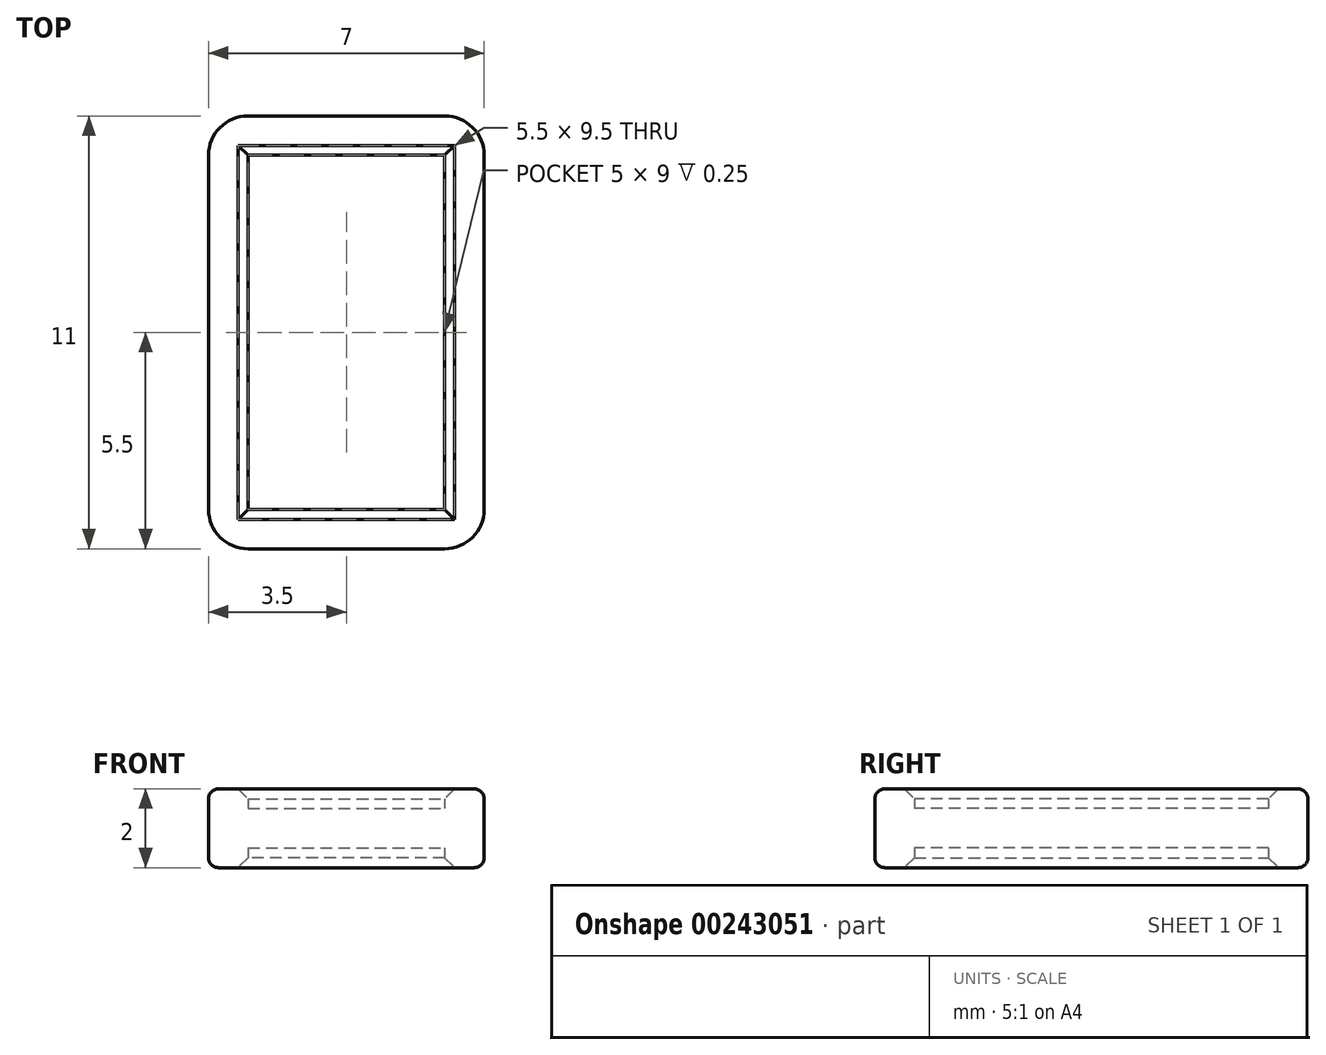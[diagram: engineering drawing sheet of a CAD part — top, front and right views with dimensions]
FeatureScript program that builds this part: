
annotation { "Feature Type Name" : "Feature", "Feature Type Description" : "" }
export const myFeature = defineFeature(function(context is Context, id is Id, definition is map)
    precondition{}
    {
        {
            var Q0;
            Q0=qCreatedBy(makeId("Top.planeOp"),FACE);
            var sketch = newSketch(context, id + "F0", { "sketchPlane" : qUnion([Q0])});
            skLineSegment(sketch, "E0.bottom", {"start": v(0, 0) * mm, "end": v(6, 0) * mm});
            skLineSegment(sketch, "E0.top", {"start": v(0, 10) * mm, "end": v(6, 10) * mm});
            skLineSegment(sketch, "E0.left", {"start": v(0, 0) * mm, "end": v(0, 10) * mm});
            skLineSegment(sketch, "E0.right", {"start": v(6, 0) * mm, "end": v(6, 10) * mm});
            skSolve(sketch);
        }
        {
            var Q0;
            Q0=makeQuery(id+"F0.imprint","IMPRINT",FACE,{"disambiguationData":[TD([[makeQuery(id+"F0.imprint","IMPRINT",EDGE,{"derivedFrom":sQuery(id+"F0.wireOp",EDGE,"E0.bottom")}),1.0]])]});
            extrude(context, id + "F1", {"entities" : qUnion([Q0]), "depth" : 1 * mm});
        }
        {
            var Q0;
            Q0=makeQuery(id+"F1.opExtrude","SWEPT_EDGE",EDGE,{"disambiguationData":[OSD([sQuery(id+"F0.wireOp",EDGE,"E0.bottom"),sQuery(id+"F0.wireOp",EDGE,"E0.right")])]});
            var Q1;
            Q1=makeQuery(id+"F1.opExtrude","SWEPT_EDGE",EDGE,{"disambiguationData":[OSD([sQuery(id+"F0.wireOp",EDGE,"E0.bottom"),sQuery(id+"F0.wireOp",EDGE,"E0.left")])]});
            var Q2;
            Q2=makeQuery(id+"F1.opExtrude","SWEPT_EDGE",EDGE,{"disambiguationData":[OSD([sQuery(id+"F0.wireOp",EDGE,"E0.top"),sQuery(id+"F0.wireOp",EDGE,"E0.right")])]});
            var Q3;
            Q3=makeQuery(id+"F1.opExtrude","SWEPT_EDGE",EDGE,{"disambiguationData":[OSD([sQuery(id+"F0.wireOp",EDGE,"E0.top"),sQuery(id+"F0.wireOp",EDGE,"E0.left")])]});
            fillet(context, id + "F2", {"entities" : qUnion([Q0, Q1, Q2, Q3]), "radius" : 0.5 * mm, "tangentPropagation" : true, "allowEdgeOverflow" : false});
        }
        {
            var Q0;
            Q0=qCreatedBy(makeId("Front.planeOp"),FACE);
            cPlane(context, id + "F3", {"entities" : qUnion([Q0]), "cplaneType" : CPlaneType.OFFSET, "offset" : 0.5 * mm, "oppositeDirection" : true, "width" : 150 * mm, "height" : 150 * mm});
        }
        {
            var Q0;
            Q0=qCreatedBy(id+"F3.planeOp",FACE);
            var sketch = newSketch(context, id + "F4", { "sketchPlane" : qUnion([Q0])});
            skLineSegment(sketch, "E1.0", {"start": v(5.5, 1) * mm, "end": v(6, 1) * mm});
            skLineSegment(sketch, "E1.1", {"start": v(6, 1) * mm, "end": v(6, 0) * mm});
            skLineSegment(sketch, "E1.2", {"start": v(6, 0) * mm, "end": v(5.5, 0) * mm});
            skLineSegment(sketch, "E2.0", {"start": v(6.5, -0.5) * mm, "end": v(5.5, -0.5) * mm});
            skLineSegment(sketch, "E2.1", {"start": v(6.5, 1.5) * mm, "end": v(6.5, -0.5) * mm});
            skLineSegment(sketch, "E2.2", {"start": v(5.5, 1.5) * mm, "end": v(6.5, 1.5) * mm});
            skLineSegment(sketch, "E3", {"start": v(5.5, 1.5) * mm, "end": v(5.5, 1) * mm});
            skLineSegment(sketch, "E4", {"start": v(5.5, 0) * mm, "end": v(5.5, -0.5) * mm});
            skSolve(sketch);
        }
        {
            var Q0;
            Q0=makeQuery(id+"F4.imprint","IMPRINT",FACE,{"disambiguationData":[TD([[makeQuery(id+"F4.imprint","IMPRINT",EDGE,{"derivedFrom":sQuery(id+"F4.wireOp",EDGE,"E1.0")}),1.0]])]});
            var Q1;
            {var subQ0=sQuery(id+"F0.wireOp",EDGE,"E0.right");var subQ1=sQuery(id+"F0.wireOp",EDGE,"E0.bottom");Q1=makeQuery(id+"F2.opFillet","BLEND_EDGE",EDGE,{"blendedFrom":[makeQuery(id+"F1.opExtrude","SWEPT_EDGE",EDGE,{"disambiguationData":[OSD([subQ1,subQ0])]}),makeQuery(id+"F1.opExtrude","CAP_FACE",FACE,{"disambiguationData":[OSD([subQ1,sQuery(id+"F0.wireOp",EDGE,"E0.top"),sQuery(id+"F0.wireOp",EDGE,"E0.left"),subQ0])],"isStart":false})],"blendedInto":[makeQuery(id+"F1.opExtrude","CAP_FACE",FACE,{"disambiguationData":[OSD([subQ1,sQuery(id+"F0.wireOp",EDGE,"E0.top"),sQuery(id+"F0.wireOp",EDGE,"E0.left"),subQ0])],"isStart":false})]});}
            var Q2;
            Q2=makeQuery(id+"F1.opExtrude","CAP_EDGE",EDGE,{"disambiguationData":[OSD([sQuery(id+"F0.wireOp",EDGE,"E0.bottom")])],"isStart":false});
            var Q3;
            {var subQ0=sQuery(id+"F0.wireOp",EDGE,"E0.left");var subQ1=sQuery(id+"F0.wireOp",EDGE,"E0.bottom");Q3=makeQuery(id+"F2.opFillet","BLEND_EDGE",EDGE,{"blendedFrom":[makeQuery(id+"F1.opExtrude","SWEPT_EDGE",EDGE,{"disambiguationData":[OSD([subQ1,subQ0])]}),makeQuery(id+"F1.opExtrude","CAP_FACE",FACE,{"disambiguationData":[OSD([subQ1,sQuery(id+"F0.wireOp",EDGE,"E0.top"),subQ0,sQuery(id+"F0.wireOp",EDGE,"E0.right")])],"isStart":false})],"blendedInto":[makeQuery(id+"F1.opExtrude","CAP_FACE",FACE,{"disambiguationData":[OSD([subQ1,sQuery(id+"F0.wireOp",EDGE,"E0.top"),subQ0,sQuery(id+"F0.wireOp",EDGE,"E0.right")])],"isStart":false})]});}
            var Q4;
            Q4=makeQuery(id+"F1.opExtrude","CAP_EDGE",EDGE,{"disambiguationData":[OSD([sQuery(id+"F0.wireOp",EDGE,"E0.left")])],"isStart":false});
            var Q5;
            {var subQ0=sQuery(id+"F0.wireOp",EDGE,"E0.left");var subQ1=sQuery(id+"F0.wireOp",EDGE,"E0.top");Q5=makeQuery(id+"F2.opFillet","BLEND_EDGE",EDGE,{"blendedFrom":[makeQuery(id+"F1.opExtrude","SWEPT_EDGE",EDGE,{"disambiguationData":[OSD([subQ1,subQ0])]}),makeQuery(id+"F1.opExtrude","CAP_FACE",FACE,{"disambiguationData":[OSD([sQuery(id+"F0.wireOp",EDGE,"E0.bottom"),subQ1,subQ0,sQuery(id+"F0.wireOp",EDGE,"E0.right")])],"isStart":false})],"blendedInto":[makeQuery(id+"F1.opExtrude","CAP_FACE",FACE,{"disambiguationData":[OSD([sQuery(id+"F0.wireOp",EDGE,"E0.bottom"),subQ1,subQ0,sQuery(id+"F0.wireOp",EDGE,"E0.right")])],"isStart":false})]});}
            var Q6;
            Q6=makeQuery(id+"F1.opExtrude","CAP_EDGE",EDGE,{"disambiguationData":[OSD([sQuery(id+"F0.wireOp",EDGE,"E0.top")])],"isStart":false});
            var Q7;
            {var subQ0=sQuery(id+"F0.wireOp",EDGE,"E0.right");var subQ1=sQuery(id+"F0.wireOp",EDGE,"E0.top");Q7=makeQuery(id+"F2.opFillet","BLEND_EDGE",EDGE,{"blendedFrom":[makeQuery(id+"F1.opExtrude","SWEPT_EDGE",EDGE,{"disambiguationData":[OSD([subQ1,subQ0])]}),makeQuery(id+"F1.opExtrude","CAP_FACE",FACE,{"disambiguationData":[OSD([sQuery(id+"F0.wireOp",EDGE,"E0.bottom"),subQ1,sQuery(id+"F0.wireOp",EDGE,"E0.left"),subQ0])],"isStart":false})],"blendedInto":[makeQuery(id+"F1.opExtrude","CAP_FACE",FACE,{"disambiguationData":[OSD([sQuery(id+"F0.wireOp",EDGE,"E0.bottom"),subQ1,sQuery(id+"F0.wireOp",EDGE,"E0.left"),subQ0])],"isStart":false})]});}
            var Q8;
            Q8=makeQuery(id+"F1.opExtrude","CAP_EDGE",EDGE,{"disambiguationData":[OSD([sQuery(id+"F0.wireOp",EDGE,"E0.right")])],"isStart":false});
            sweep(context, id + "F5", {"operationType" : NewBodyOperationType.ADD, "profiles" : qUnion([Q0]), "path" : qUnion([Q1, Q2, Q3, Q4, Q5, Q6, Q7, Q8])});
        }
        {
            var Q0;
            Q0=makeQuery(id+"F5.opSweep","SWEPT_EDGE",EDGE,{"disambiguationData":[OSD([sQuery(id+"F0.wireOp",EDGE,"E0.bottom"),sQuery(id+"F4.wireOp",EDGE,"E2.0"),sQuery(id+"F4.wireOp",EDGE,"E2.1")])]});
            var Q1;
            Q1=makeQuery(id+"F5.opSweep","SWEPT_EDGE",EDGE,{"disambiguationData":[OSD([sQuery(id+"F0.wireOp",EDGE,"E0.left"),sQuery(id+"F4.wireOp",EDGE,"E2.1"),sQuery(id+"F4.wireOp",EDGE,"E2.2")])]});
            fillet(context, id + "F6", {"entities" : qUnion([Q0, Q1]), "radius" : .25 * mm, "tangentPropagation" : true, "allowEdgeOverflow" : false});
        }
        {
            var Q0;
            Q0=makeQuery(id+"F5.opSweep","SWEPT_EDGE",EDGE,{"disambiguationData":[OSD([sQuery(id+"F0.wireOp",EDGE,"E0.left"),sQuery(id+"F4.wireOp",EDGE,"E2.2"),sQuery(id+"F4.wireOp",EDGE,"E3")])]});
            var Q1;
            Q1=makeQuery(id+"F5.opSweep","SWEPT_EDGE",EDGE,{"disambiguationData":[OSD([sQuery(id+"F0.wireOp",EDGE,"E0.top"),sQuery(id+"F4.wireOp",EDGE,"E2.2"),sQuery(id+"F4.wireOp",EDGE,"E3")])]});
            var Q2;
            Q2=makeQuery(id+"F5.opSweep","SWEPT_EDGE",EDGE,{"disambiguationData":[OSD([sQuery(id+"F0.wireOp",EDGE,"E0.right"),sQuery(id+"F4.wireOp",EDGE,"E2.2"),sQuery(id+"F4.wireOp",EDGE,"E3")])]});
            var Q3;
            Q3=makeQuery(id+"F5.opSweep","SWEPT_EDGE",EDGE,{"disambiguationData":[OSD([sQuery(id+"F0.wireOp",EDGE,"E0.bottom"),sQuery(id+"F4.wireOp",EDGE,"E2.2"),sQuery(id+"F4.wireOp",EDGE,"E3")])]});
            var Q4;
            Q4=makeQuery(id+"F5.opSweep","SWEPT_EDGE",EDGE,{"disambiguationData":[OSD([sQuery(id+"F0.wireOp",EDGE,"E0.right"),sQuery(id+"F4.wireOp",EDGE,"E2.0"),sQuery(id+"F4.wireOp",EDGE,"E4")])]});
            var Q5;
            Q5=makeQuery(id+"F5.opSweep","SWEPT_EDGE",EDGE,{"disambiguationData":[OSD([sQuery(id+"F0.wireOp",EDGE,"E0.bottom"),sQuery(id+"F4.wireOp",EDGE,"E2.0"),sQuery(id+"F4.wireOp",EDGE,"E4")])]});
            var Q6;
            Q6=makeQuery(id+"F5.opSweep","SWEPT_EDGE",EDGE,{"disambiguationData":[OSD([sQuery(id+"F0.wireOp",EDGE,"E0.left"),sQuery(id+"F4.wireOp",EDGE,"E2.0"),sQuery(id+"F4.wireOp",EDGE,"E4")])]});
            var Q7;
            Q7=makeQuery(id+"F5.opSweep","SWEPT_EDGE",EDGE,{"disambiguationData":[OSD([sQuery(id+"F0.wireOp",EDGE,"E0.top"),sQuery(id+"F4.wireOp",EDGE,"E2.0"),sQuery(id+"F4.wireOp",EDGE,"E4")])]});
            chamfer(context, id + "F7", {"entities" : qUnion([Q0, Q1, Q2, Q3, Q4, Q5, Q6, Q7]), "width" : .25 * mm, "tangentPropagation" : true});
        }
    });
